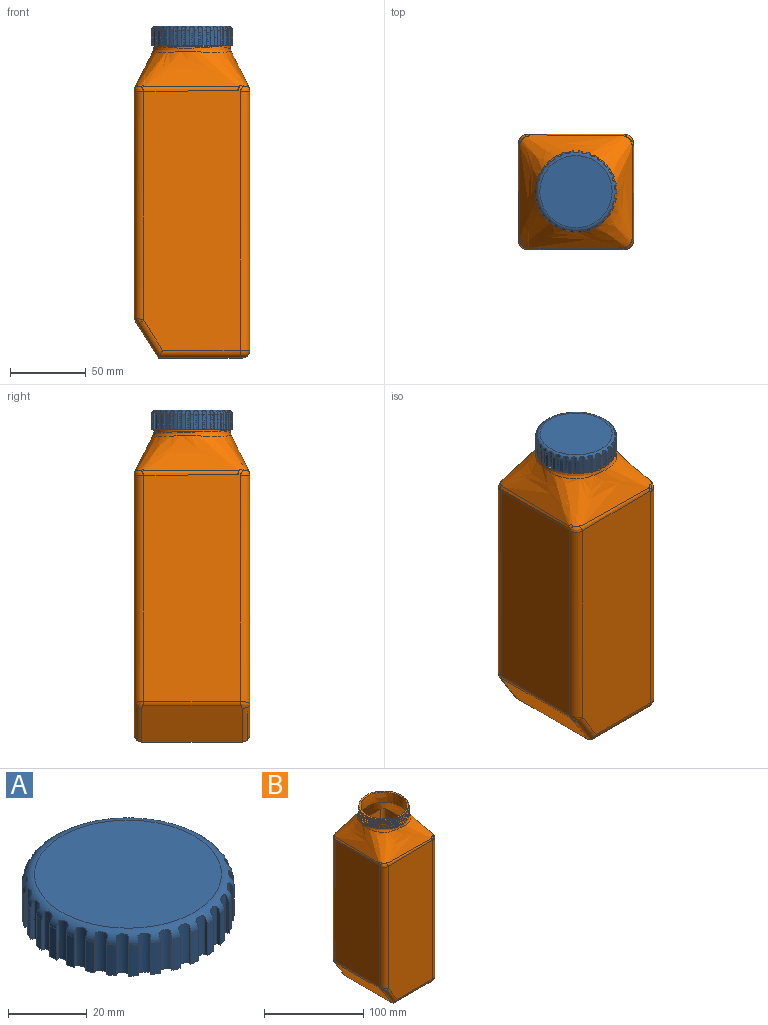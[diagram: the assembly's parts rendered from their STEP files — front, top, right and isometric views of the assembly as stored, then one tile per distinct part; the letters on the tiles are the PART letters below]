
ASSEMBLY  parts=2 mates=1
PART A: 131 faces, bbox 58.5x58.5x12.9 mm
  f0: cylinder r=26.99mm len=9.53mm, axis (0,0,-1), area 23.6mm2, adj f31,f40,f126,f128
  f1: cylinder r=26.99mm len=9.53mm, axis (0,0,-1), area 23.6mm2, adj f31,f40,f123,f125
  f2: cylinder r=26.99mm len=9.53mm, axis (0,0,-1), area 23.6mm2, adj f31,f40,f120,f122
  f3: cylinder r=26.99mm len=9.53mm, axis (0,0,-1), area 23.6mm2, adj f31,f40,f117,f119
  f4: cylinder r=26.99mm len=9.53mm, axis (0,0,-1), area 23.6mm2, adj f31,f40,f114,f116
  f5: cylinder r=26.99mm len=9.53mm, axis (0,0,-1), area 23.6mm2, adj f31,f40,f111,f113
  f6: cylinder r=26.99mm len=9.53mm, axis (0,0,-1), area 23.6mm2, adj f31,f40,f108,f110
  f7: cylinder r=26.99mm len=9.53mm, axis (0,0,-1), area 23.6mm2, adj f31,f40,f105,f107
  f8: cylinder r=26.99mm len=9.53mm, axis (0,0,-1), area 23.6mm2, adj f31,f40,f102,f104
  f9: cylinder r=26.99mm len=9.53mm, axis (0,0,-1), area 23.6mm2, adj f31,f40,f99,f101
  f10: cylinder r=26.99mm len=9.53mm, axis (0,0,-1), area 23.6mm2, adj f31,f40,f96,f98
  f11: cylinder r=26.99mm len=9.53mm, axis (0,0,-1), area 23.6mm2, adj f31,f40,f93,f95
  f12: cylinder r=26.99mm len=9.53mm, axis (0,0,-1), area 23.6mm2, adj f31,f40,f90,f92
  f13: cylinder r=26.99mm len=9.53mm, axis (0,0,-1), area 23.6mm2, adj f31,f40,f87,f89
  f14: cylinder r=26.99mm len=9.53mm, axis (0,0,-1), area 23.6mm2, adj f31,f40,f84,f86
  f15: cylinder r=26.99mm len=9.53mm, axis (0,0,-1), area 23.6mm2, adj f31,f40,f81,f83
  f16: cylinder r=26.99mm len=9.53mm, axis (0,0,-1), area 23.6mm2, adj f31,f40,f78,f80
  f17: cylinder r=26.99mm len=9.53mm, axis (0,0,-1), area 23.6mm2, adj f31,f40,f75,f77
  f18: cylinder r=26.99mm len=9.53mm, axis (0,0,-1), area 23.6mm2, adj f31,f40,f72,f74
  f19: cylinder r=26.99mm len=9.53mm, axis (0,0,-1), area 23.6mm2, adj f31,f40,f69,f71
  f20: cylinder r=26.99mm len=9.53mm, axis (0,0,-1), area 23.6mm2, adj f31,f40,f66,f68
  f21: cylinder r=26.99mm len=9.53mm, axis (0,0,-1), area 23.6mm2, adj f31,f40,f63,f65
  f22: cylinder r=26.99mm len=9.53mm, axis (0,0,-1), area 23.6mm2, adj f31,f40,f60,f62
  f23: cylinder r=26.99mm len=9.53mm, axis (0,0,-1), area 23.6mm2, adj f31,f40,f57,f59
  f24: cylinder r=26.99mm len=9.53mm, axis (0,0,-1), area 23.6mm2, adj f31,f40,f54,f56
  f25: cylinder r=26.99mm len=9.53mm, axis (0,0,-1), area 23.6mm2, adj f31,f40,f51,f53
  f26: cylinder r=26.99mm len=9.53mm, axis (0,0,-1), area 23.6mm2, adj f31,f40,f48,f50
  f27: cylinder r=26.99mm len=9.53mm, axis (0,0,-1), area 23.6mm2, adj f31,f40,f45,f47
  f28: cylinder r=26.99mm len=9.53mm, axis (0,0,-1), area 23.6mm2, adj f31,f40,f42,f44
  f29: cylinder r=26.99mm len=9.53mm, axis (0,0,-1), area 23.6mm2, adj f31,f40,f41,f129
  f30: plane 47.63x47.63mm, normal (0,0,1), area 1781.4mm2, adj f40
  f31: plane 53.98x53.88mm, normal (0,0,-1), area 314.8mm2, adj f0,f1,f2,f3,f4,f5,f6,f7
  f32: cylinder r=23.81mm len=47.63mm, axis (0,0,-1), area 553.3mm2, adj f31,f33,f35,f36,f38,f39
  f33: plane 47.63x47.63mm, normal (0,0,-1), area 1771.7mm2, adj f32,f37,f38,f39
  f34: cylinder r=24.61mm len=49.21mm, axis (0,0,-1), area 930.4mm2, adj f31,f35,f36,f38,f39
  f35: plane 0.79x0.2mm, normal (0,1,0), area 0.2mm2, adj f31,f32,f34,f39
  f36: bspline ~56.83x49.21mm, area 413.5mm2, adj f31,f32,f34,f38
  f37: cylinder r=23.02mm len=11.51mm, axis (0,0,-1), area 1.2mm2, adj f33,f38,f39
  f38: plane 1.59x1.59mm, normal (0,-1,0), area 1.4mm2, adj f32,f33,f34,f36,f37,f39
  f39: bspline ~56.83x49.21mm, area 492mm2, adj f32,f33,f34,f35,f37,f38
  f40: torus R=23.81mm, axis (0,0,1), area 527.2mm2, adj f0,f1,f2,f3,f4,f5,f6,f7
  f41: plane 11.84x1mm, normal (1,0,0), area 10.8mm2, adj f29,f31,f40,f43
  f42: plane 11.84x1mm, normal (-1,0,0), area 10.8mm2, adj f28,f31,f40,f43
  f43: cylinder r=3.29mm len=12.17mm, axis (0,0,-1), area 39.9mm2, adj f31,f40,f41,f42
  f44: plane 11.84x0.98mm, normal (0.98,0.21,0), area 10.8mm2, adj f28,f31,f40,f46
  f45: plane 11.84x0.98mm, normal (-0.98,-0.21,0), area 10.8mm2, adj f27,f31,f40,f46
  f46: cylinder r=3.29mm len=12.17mm, axis (0,0,-1), area 39.9mm2, adj f31,f40,f44,f45
  f47: plane 11.84x0.91mm, normal (0.91,0.41,0), area 10.8mm2, adj f27,f31,f40,f49
  f48: plane 11.84x0.91mm, normal (-0.91,-0.41,0), area 10.8mm2, adj f26,f31,f40,f49
  f49: cylinder r=3.29mm len=12.17mm, axis (0,0,-1), area 39.9mm2, adj f31,f40,f47,f48
  f50: plane 11.84x0.81mm, normal (0.81,0.59,0), area 10.8mm2, adj f26,f31,f40,f52
  f51: plane 11.84x0.81mm, normal (-0.81,-0.59,0), area 10.8mm2, adj f25,f31,f40,f52
  f52: cylinder r=3.29mm len=12.17mm, axis (0,0,-1), area 39.9mm2, adj f31,f40,f50,f51
  f53: plane 11.84x0.75mm, normal (0.67,0.74,0), area 10.8mm2, adj f25,f31,f40,f55
  f54: plane 11.84x0.75mm, normal (-0.67,-0.74,0), area 10.8mm2, adj f24,f31,f40,f55
  f55: cylinder r=3.29mm len=12.17mm, axis (0,0,-1), area 39.9mm2, adj f31,f40,f53,f54
  f56: plane 11.84x0.87mm, normal (0.5,0.87,0), area 10.8mm2, adj f24,f31,f40,f58
  f57: plane 11.84x0.87mm, normal (-0.5,-0.87,0), area 10.8mm2, adj f23,f31,f40,f58
  f58: cylinder r=3.29mm len=12.17mm, axis (0,0,-1), area 39.9mm2, adj f31,f40,f56,f57
  f59: plane 11.84x0.95mm, normal (0.31,0.95,0), area 10.8mm2, adj f23,f31,f40,f61
  f60: plane 11.84x0.95mm, normal (-0.31,-0.95,0), area 10.8mm2, adj f22,f31,f40,f61
  f61: cylinder r=3.29mm len=12.17mm, axis (0,0,-1), area 39.9mm2, adj f31,f40,f59,f60
  f62: plane 11.84x0.99mm, normal (0.1,0.99,0), area 10.8mm2, adj f22,f31,f40,f64
  f63: plane 11.84x0.99mm, normal (-0.1,-0.99,0), area 10.8mm2, adj f21,f31,f40,f64
  f64: cylinder r=3.29mm len=12.17mm, axis (0,0,-1), area 39.9mm2, adj f31,f40,f62,f63
  f65: plane 11.84x0.99mm, normal (-0.1,0.99,0), area 10.8mm2, adj f21,f31,f40,f67
  f66: plane 11.84x0.99mm, normal (0.1,-0.99,0), area 10.8mm2, adj f20,f31,f40,f67
  f67: cylinder r=3.29mm len=12.17mm, axis (0,0,-1), area 39.9mm2, adj f31,f40,f65,f66
  f68: plane 11.84x0.95mm, normal (-0.31,0.95,0), area 10.8mm2, adj f20,f31,f40,f70
  f69: plane 11.84x0.95mm, normal (0.31,-0.95,0), area 10.8mm2, adj f19,f31,f40,f70
  f70: cylinder r=3.29mm len=12.17mm, axis (0,0,-1), area 39.9mm2, adj f31,f40,f68,f69
  f71: plane 11.84x0.87mm, normal (-0.5,0.87,0), area 10.8mm2, adj f19,f31,f40,f73
  f72: plane 11.84x0.87mm, normal (0.5,-0.87,0), area 10.8mm2, adj f18,f31,f40,f73
  f73: cylinder r=3.29mm len=12.17mm, axis (0,0,-1), area 39.9mm2, adj f31,f40,f71,f72
  f74: plane 11.84x0.75mm, normal (-0.67,0.74,0), area 10.8mm2, adj f18,f31,f40,f76
  f75: plane 11.84x0.75mm, normal (0.67,-0.74,0), area 10.8mm2, adj f17,f31,f40,f76
  f76: cylinder r=3.29mm len=12.17mm, axis (0,0,-1), area 39.9mm2, adj f31,f40,f74,f75
  f77: plane 11.84x0.81mm, normal (-0.81,0.59,0), area 10.8mm2, adj f17,f31,f40,f79
  f78: plane 11.84x0.81mm, normal (0.81,-0.59,0), area 10.8mm2, adj f16,f31,f40,f79
  f79: cylinder r=3.29mm len=12.17mm, axis (0,0,-1), area 39.9mm2, adj f31,f40,f77,f78
  f80: plane 11.84x0.91mm, normal (-0.91,0.41,0), area 10.8mm2, adj f16,f31,f40,f82
  f81: plane 11.84x0.91mm, normal (0.91,-0.41,0), area 10.8mm2, adj f15,f31,f40,f82
  f82: cylinder r=3.29mm len=12.17mm, axis (0,0,-1), area 39.9mm2, adj f31,f40,f80,f81
  f83: plane 11.84x0.98mm, normal (-0.98,0.21,0), area 10.8mm2, adj f15,f31,f40,f85
  f84: plane 11.84x0.98mm, normal (0.98,-0.21,0), area 10.8mm2, adj f14,f31,f40,f85
  f85: cylinder r=3.29mm len=12.17mm, axis (0,0,-1), area 39.9mm2, adj f31,f40,f83,f84
  f86: plane 11.84x1mm, normal (-1,0,0), area 10.8mm2, adj f14,f31,f40,f88
  f87: plane 11.84x1mm, normal (1,0,0), area 10.8mm2, adj f13,f31,f40,f88
  f88: cylinder r=3.29mm len=12.17mm, axis (0,0,-1), area 39.9mm2, adj f31,f40,f86,f87
  f89: plane 11.84x0.98mm, normal (-0.98,-0.21,0), area 10.8mm2, adj f13,f31,f40,f91
  f90: plane 11.84x0.98mm, normal (0.98,0.21,0), area 10.8mm2, adj f12,f31,f40,f91
  f91: cylinder r=3.29mm len=12.17mm, axis (0,0,-1), area 39.9mm2, adj f31,f40,f89,f90
  f92: plane 11.84x0.91mm, normal (-0.91,-0.41,0), area 10.8mm2, adj f12,f31,f40,f94
  f93: plane 11.84x0.91mm, normal (0.91,0.41,0), area 10.8mm2, adj f11,f31,f40,f94
  f94: cylinder r=3.29mm len=12.17mm, axis (0,0,-1), area 39.9mm2, adj f31,f40,f92,f93
  f95: plane 11.84x0.81mm, normal (-0.81,-0.59,0), area 10.8mm2, adj f11,f31,f40,f97
  f96: plane 11.84x0.81mm, normal (0.81,0.59,0), area 10.8mm2, adj f10,f31,f40,f97
  f97: cylinder r=3.29mm len=12.17mm, axis (0,0,-1), area 39.9mm2, adj f31,f40,f95,f96
  f98: plane 11.84x0.75mm, normal (-0.67,-0.74,0), area 10.8mm2, adj f10,f31,f40,f100
  f99: plane 11.84x0.75mm, normal (0.67,0.74,0), area 10.8mm2, adj f9,f31,f40,f100
  f100: cylinder r=3.29mm len=12.17mm, axis (0,0,-1), area 39.9mm2, adj f31,f40,f98,f99
  f101: plane 11.84x0.87mm, normal (-0.5,-0.87,0), area 10.8mm2, adj f9,f31,f40,f103
  f102: plane 11.84x0.87mm, normal (0.5,0.87,0), area 10.8mm2, adj f8,f31,f40,f103
  f103: cylinder r=3.29mm len=12.17mm, axis (0,0,-1), area 39.9mm2, adj f31,f40,f101,f102
  f104: plane 11.84x0.95mm, normal (-0.31,-0.95,0), area 10.8mm2, adj f8,f31,f40,f106
  f105: plane 11.84x0.95mm, normal (0.31,0.95,0), area 10.8mm2, adj f7,f31,f40,f106
  f106: cylinder r=3.29mm len=12.17mm, axis (0,0,-1), area 39.9mm2, adj f31,f40,f104,f105
  f107: plane 11.84x0.99mm, normal (-0.1,-0.99,0), area 10.8mm2, adj f7,f31,f40,f109
  f108: plane 11.84x0.99mm, normal (0.1,0.99,0), area 10.8mm2, adj f6,f31,f40,f109
  f109: cylinder r=3.29mm len=12.17mm, axis (0,0,-1), area 39.9mm2, adj f31,f40,f107,f108
  f110: plane 11.84x0.99mm, normal (0.1,-0.99,0), area 10.8mm2, adj f6,f31,f40,f112
  f111: plane 11.84x0.99mm, normal (-0.1,0.99,0), area 10.8mm2, adj f5,f31,f40,f112
  f112: cylinder r=3.29mm len=12.17mm, axis (0,0,-1), area 39.9mm2, adj f31,f40,f110,f111
  f113: plane 11.84x0.95mm, normal (0.31,-0.95,0), area 10.8mm2, adj f5,f31,f40,f115
  f114: plane 11.84x0.95mm, normal (-0.31,0.95,0), area 10.8mm2, adj f4,f31,f40,f115
  f115: cylinder r=3.29mm len=12.17mm, axis (0,0,-1), area 39.9mm2, adj f31,f40,f113,f114
  f116: plane 11.84x0.87mm, normal (0.5,-0.87,0), area 10.8mm2, adj f4,f31,f40,f118
  f117: plane 11.84x0.87mm, normal (-0.5,0.87,0), area 10.8mm2, adj f3,f31,f40,f118
  f118: cylinder r=3.29mm len=12.17mm, axis (0,0,-1), area 39.9mm2, adj f31,f40,f116,f117
  f119: plane 11.84x0.75mm, normal (0.67,-0.74,0), area 10.8mm2, adj f3,f31,f40,f121
  f120: plane 11.84x0.75mm, normal (-0.67,0.74,0), area 10.8mm2, adj f2,f31,f40,f121
  f121: cylinder r=3.29mm len=12.17mm, axis (0,0,-1), area 39.9mm2, adj f31,f40,f119,f120
  f122: plane 11.84x0.81mm, normal (0.81,-0.59,0), area 10.8mm2, adj f2,f31,f40,f124
  f123: plane 11.84x0.81mm, normal (-0.81,0.59,0), area 10.8mm2, adj f1,f31,f40,f124
  f124: cylinder r=3.29mm len=12.17mm, axis (0,0,-1), area 39.9mm2, adj f31,f40,f122,f123
  f125: plane 11.84x0.91mm, normal (0.91,-0.41,0), area 10.8mm2, adj f1,f31,f40,f127
  f126: plane 11.84x0.91mm, normal (-0.91,0.41,0), area 10.8mm2, adj f0,f31,f40,f127
  f127: cylinder r=3.29mm len=12.17mm, axis (0,0,-1), area 39.9mm2, adj f31,f40,f125,f126
  f128: plane 11.84x0.98mm, normal (0.98,-0.21,0), area 10.8mm2, adj f0,f31,f40,f130
  f129: plane 11.84x0.98mm, normal (-0.98,0.21,0), area 10.8mm2, adj f29,f31,f40,f130
  f130: cylinder r=3.29mm len=12.17mm, axis (0,0,-1), area 39.9mm2, adj f31,f40,f128,f129
PART B: 59 faces, bbox 79.9x80.4x219.4 mm
  f0: cylinder r=25.4mm len=50.8mm, axis (0,0,-1), area 826.3mm2, adj f1,f41,f53,f54,f55,f56,f57
  f1: bspline ~51.82x51.81mm, area 437.3mm2, adj f0,f11,f40,f55,f56
  f2: plane 66.04x55.25mm, normal (0,0,-1), area 3647.7mm2, adj f12,f13,f15,f17,f19,f21
  f3: plane 149.74x63.5mm, normal (-1,0,0), area 9500mm2, adj f8,f9,f18,f27,f31
  f4: cylinder r=6.35mm len=170.81mm, axis (0,0,1), area 1703.4mm2, adj f5,f10,f15,f28
  f5: plane 171.52x63.5mm, normal (1,0,0), area 10882.8mm2, adj f4,f6,f17,f30,f34
  f6: cylinder r=6.35mm len=170.81mm, axis (0,0,1), area 1703.4mm2, adj f5,f7,f19,f36
  f7: plane 171.52x63.5mm, normal (0,1,0), area 10760.9mm2, adj f6,f8,f21,f22,f35,f38
  f8: cylinder r=6.35mm len=151.07mm, axis (0,0,1), area 1496.4mm2, adj f3,f7,f20,f33
  f9: cylinder r=6.35mm len=151.07mm, axis (0,0,1), area 1496.4mm2, adj f3,f10,f16,f25
  f10: plane 171.52x63.5mm, normal (0,-1,0), area 10761.6mm2, adj f4,f9,f13,f14,f23,f26
  f11: bspline ~75.13x75.13mm, area 6181.7mm2, adj f1,f23,f24,f25,f26,f27,f28,f29
  f12: plane 66.04x24.16mm, normal (-0.85,0,-0.53), area 1880.6mm2, adj f2,f14,f16,f18,f20,f22
  f13: cylinder r=5.08mm len=53.98mm, axis (1,0,0), area 419.5mm2, adj f2,f10,f14,f15
  f14: cylinder r=5.08mm len=24.83mm, axis (-0.53,0,0.85), area 197mm2, adj f10,f12,f13,f16
  f15: torus R=1.27mm, axis (0,0,1), area 56.5mm2, adj f2,f4,f13,f17
  f16: bspline ~7.45x7.08mm, area 29.9mm2, adj f9,f12,f14,f18
  f17: cylinder r=5.08mm len=63.5mm, axis (0,-1,0), area 506.7mm2, adj f2,f5,f15,f19
  f18: cylinder r=5.08mm len=63.5mm, axis (0,-1,0), area 180.2mm2, adj f3,f12,f16,f20
  f19: torus R=1.27mm, axis (0,0,1), area 56.5mm2, adj f2,f6,f17,f21
  f20: bspline ~6.35x6.35mm, area 29.9mm2, adj f8,f12,f18,f22
  f21: cylinder r=5.08mm len=53.98mm, axis (1,0,0), area 419.5mm2, adj f2,f7,f19,f22
  f22: cylinder r=5.08mm len=24.83mm, axis (-0.53,0,0.85), area 197mm2, adj f7,f12,f20,f21
  f23: bspline ~64.73x3.75mm, area 166mm2, adj f10,f11,f24,f25
  f24: bspline ~3.16x1.23mm, area 0.6mm2, adj f11,f23,f26
  f25: bspline ~8.31x8.09mm, area 30mm2, adj f9,f11,f23,f27
  f26: bspline ~4.34x4.25mm, area 8.7mm2, adj f10,f11,f24,f28
  f27: bspline ~4.13x4.05mm, area 8.7mm2, adj f3,f11,f25,f29
  f28: bspline ~8.31x8.09mm, area 30mm2, adj f4,f11,f26,f30
  f29: bspline ~3.16x1.23mm, area 0.6mm2, adj f11,f27,f31
  f30: bspline ~65.61x4.04mm, area 165.9mm2, adj f5,f11,f28,f32
  f31: bspline ~65.61x4.04mm, area 165.9mm2, adj f3,f11,f29,f33
  f32: bspline ~3.16x1.23mm, area 0.6mm2, adj f11,f30,f34
  f33: bspline ~8.31x8.09mm, area 30mm2, adj f8,f11,f31,f35
  f34: bspline ~4.13x4.05mm, area 8.7mm2, adj f5,f11,f32,f36
  f35: bspline ~4.13x4.05mm, area 8.7mm2, adj f7,f11,f33,f37
  f36: bspline ~8.31x8.09mm, area 30mm2, adj f6,f11,f34,f38
  f37: bspline ~3.16x1.23mm, area 0.6mm2, adj f11,f35,f38
  f38: bspline ~65.61x4.04mm, area 165.9mm2, adj f7,f11,f36,f37
  f39: extruded ~47.22x47.21mm, area 1871mm2, adj f41,f52
  f40: cylinder r=25.4mm len=17.55mm, axis (0,0,-1), area 2.6mm2, adj f1,f56
  f41: plane 50.8x50.62mm, normal (0,0,1), area 271.1mm2, adj f0,f39,f54,f57,f58
  f42: plane 73.03x57.86mm, normal (0,0,1), area 4215.3mm2, adj f43,f44,f45,f46,f47,f51
  f43: plane 76.23x27.47mm, normal (0.85,0,0.53), area 2071.4mm2, adj f42,f47,f48,f49,f50,f51
  f44: cylinder r=4.76mm len=175.8mm, axis (0,0,1), area 1314.7mm2, adj f42,f45,f51,f52
  f45: plane 175.84x63.5mm, normal (-1,0,0), area 11163.2mm2, adj f42,f44,f46,f52
  f46: cylinder r=4.76mm len=175.8mm, axis (0,0,1), area 1314.7mm2, adj f42,f45,f47,f52
  f47: plane 175.84x63.5mm, normal (0,-1,0), area 11076.6mm2, adj f42,f43,f46,f48,f52
  f48: cylinder r=4.76mm len=159.15mm, axis (0,0,1), area 1161.7mm2, adj f43,f47,f49,f52
  f49: plane 151.57x63.5mm, normal (1,0,0), area 9622.2mm2, adj f43,f48,f50,f52
  f50: cylinder r=4.76mm len=159.15mm, axis (0,0,1), area 1161.7mm2, adj f43,f49,f51,f52
  f51: plane 175.97x63.63mm, normal (0,1,0), area 11076.5mm2, adj f42,f43,f44,f50,f52
  f52: offset ~79.09x79.09mm, area 6910.2mm2, adj f39,f44,f45,f46,f47,f48,f49,f50
  f53: bspline ~9.67x6.54mm, area 0mm2, adj f0,f57
  f54: plane 0.79x0.79mm, normal (0,-1,0), area 0.6mm2, adj f0,f41,f56,f58
  f55: plane 1.59x0.9mm, normal (0,1,0), area 1.3mm2, adj f0,f1,f56,f57,f58
  f56: bspline ~60.49x52.39mm, area 502mm2, adj f0,f1,f40,f54,f55,f58
  f57: bspline ~60.49x52.39mm, area 465.5mm2, adj f0,f41,f53,f55,f58
  f58: cylinder r=24.61mm len=49.21mm, axis (0,0,-1), area 961.1mm2, adj f41,f54,f55,f56,f57
PLACE A t=(0,0,206.38)mm
PLACE B at identity
MATE cylindrical A.f0 <-> B.f0  axis (0,0,-1) through (0,0,215.9)mm
